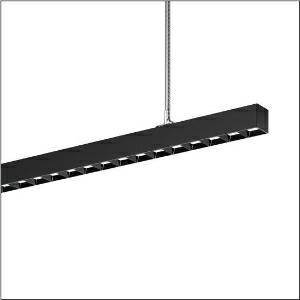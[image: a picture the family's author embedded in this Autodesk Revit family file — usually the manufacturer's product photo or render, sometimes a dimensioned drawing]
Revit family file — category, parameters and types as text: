
# Revit family: silica_21_51mx31dc3dbb
name_source: partatom
category: Lighting Fixtures
units: mm (PartAtom-declared; Revit-internal decimal feet)

## family parameters
Cut with Voids When Loaded = No
Host = Face
Light Source = No
Part Type = Normal
Room Calculation Point = No
Round Connector Dimension = Use Diameter
Shared = No

## types (1)
- --- (1 x LED, 18230 lm, 113.3 W, 3000K)
    Apparent Load = 113 VA
    CIE Flux Codes = 87 99 100 59 100
    Color Rendering = 80
    Color Temperature = 3000K
    Default Elevation = 1800 mm
    Description = Silica 21, office luminaire, primary light control with darklight reflector, of PMMA, black, CAT 2 (L<= 3000cd/m²), light emission: direct/indirect distribution, primary light characteristic: symmetric, installation type: suspended mounting, LED, rated luminous flux: 18.230lm, luminous efficacy: 161lm/W, light colour: 830, colour temperature: 3000K, control gear: DALI 2, with terminal, 3+2-pole, max. 2.5mm², mains connection: 220..240V, AC, 50/60Hz, rated input power: 113.3W, luminaire housing, of aluminium, matt jet black (RAL 9005), length: 3.004mm, width: 53mm, height: 53mm, protection rating (complete): IP20, insulation class (complete): insulation class I (protective earthing), certification: CE, permissible operating ambient temperature: 0..+35°C, standard: EN 50419, packaging unit: 1 piece
    Height = 53 mm
    Lamp = 1 x LED
    Lamp Light Flux = 18230 lm
    Lamp Power = 113.3 W
    Lamp count = 1
    Length = 3004 mm
    Luminous efficacy = 161 lm/W
    Manufacturer = Siteco
    ModVariant = No
    Model = 51MX31DC3DBB
    Mounting Place = Ceiling
    Mounting Type = Pendant
    Number of Poles = 1
    OnlyDefault = Yes
    Power Factor = 1
    Product Name = Silica 21
    Product group = office luminaire | ceiling pendant
    ProductGroupID = 903
    Protection Class = Protection class I
    Protection Degree = IP 20
    RLX_Detail_Level = 1
    RLX_Emergency_Light_Flux = 0 lm
    RLX_Emergency_Type = 0
    RLX_Emergency_Type_DB = No
    RlxData = <blob elided: 66561 chars, md5=a9469b6e>
    Socket = socket
    Standby Power = 0 W
    System Light Flux = 18230 lm
    System Power = 113 W
    Type Comments = factory setting: luminous flux: 100 % | dim-lin: 254 | 392 mA
    Type Image = l_1335852.jpg
    URL = http://relux.com
    VarID = @adj_121227
    Voltage = 0 V
    Weight = 0.00 kg
    Width = 53 mm

## geometry (parser evidence)
native form markers: Blend x4, Sweep x14
no freeform markers — native parametric forms only
